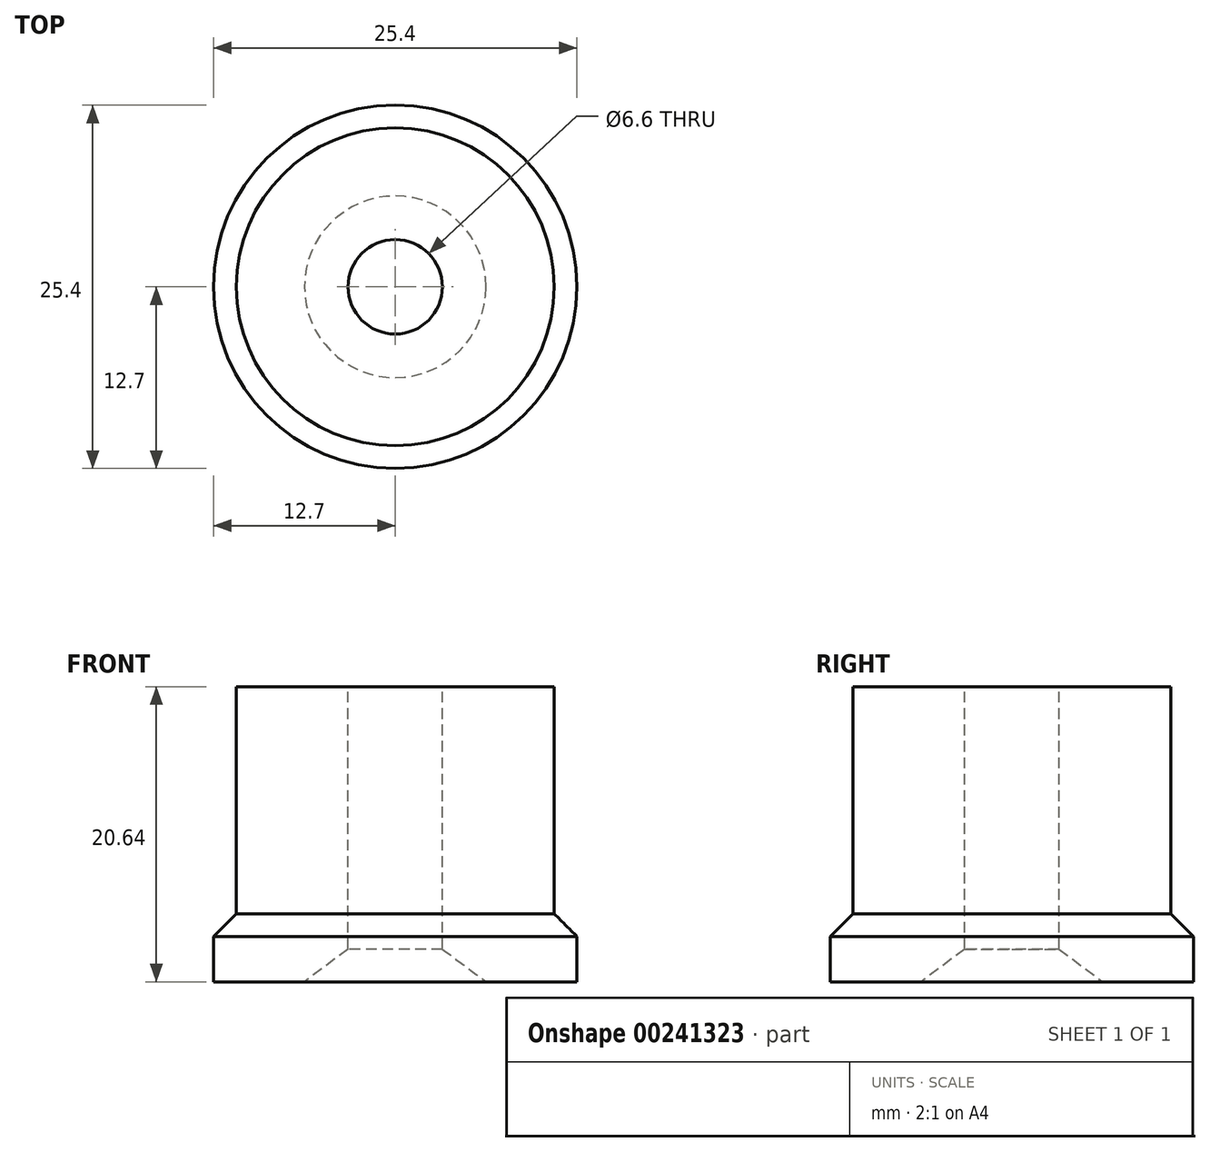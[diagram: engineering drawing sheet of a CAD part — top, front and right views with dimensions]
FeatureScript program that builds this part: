
annotation { "Feature Type Name" : "Feature", "Feature Type Description" : "" }
export const myFeature = defineFeature(function(context is Context, id is Id, definition is map)
    precondition{}
    {
        {
            var Q0;
            Q0=qCreatedBy(makeId("Front.planeOp"),FACE);
            var sketch = newSketch(context, id + "F0", { "sketchPlane" : qUnion([Q0])});
            skLineSegment(sketch, "E0", {"start": v(-6.35, 0) * mm, "end": v(-12.7, 0) * mm});
            skLineSegment(sketch, "E1", {"start": v(-12.7, 0) * mm, "end": v(-12.7, 3.18) * mm});
            skLineSegment(sketch, "E2", {"start": v(-12.7, 3.17) * mm, "end": v(-11.11, 4.76) * mm});
            skLineSegment(sketch, "E3", {"start": v(-11.11, 4.76) * mm, "end": v(-11.11, 20.64) * mm});
            skLineSegment(sketch, "E4", {"start": v(-11.11, 20.64) * mm, "end": v(-3.3, 20.64) * mm});
            skLineSegment(sketch, "E5", {"start": v(0, 20.64) * mm, "end": v(0, 4.76) * mm});
            skLineSegment(sketch, "E6", {"start": v(-3.3, 2.29) * mm, "end": v(-6.35, 0) * mm});
            skLineSegment(sketch, "E7.0", {"start": v(-3.3, 20.64) * mm, "end": v(-3.3, 2.29) * mm});
            skSolve(sketch);
        }
        {
            var Q0;
            Q0 = qSketchRegion(id + "F0", true);
            var Q1;
            Q1=sQuery(id+"F0.wireOp",EDGE,"E5");
            revolve(context, id + "F1", {"entities" : qUnion([Q0]), "axis" : qUnion([Q1]), "revolveType" : RevolveType.FULL});
        }
    });
